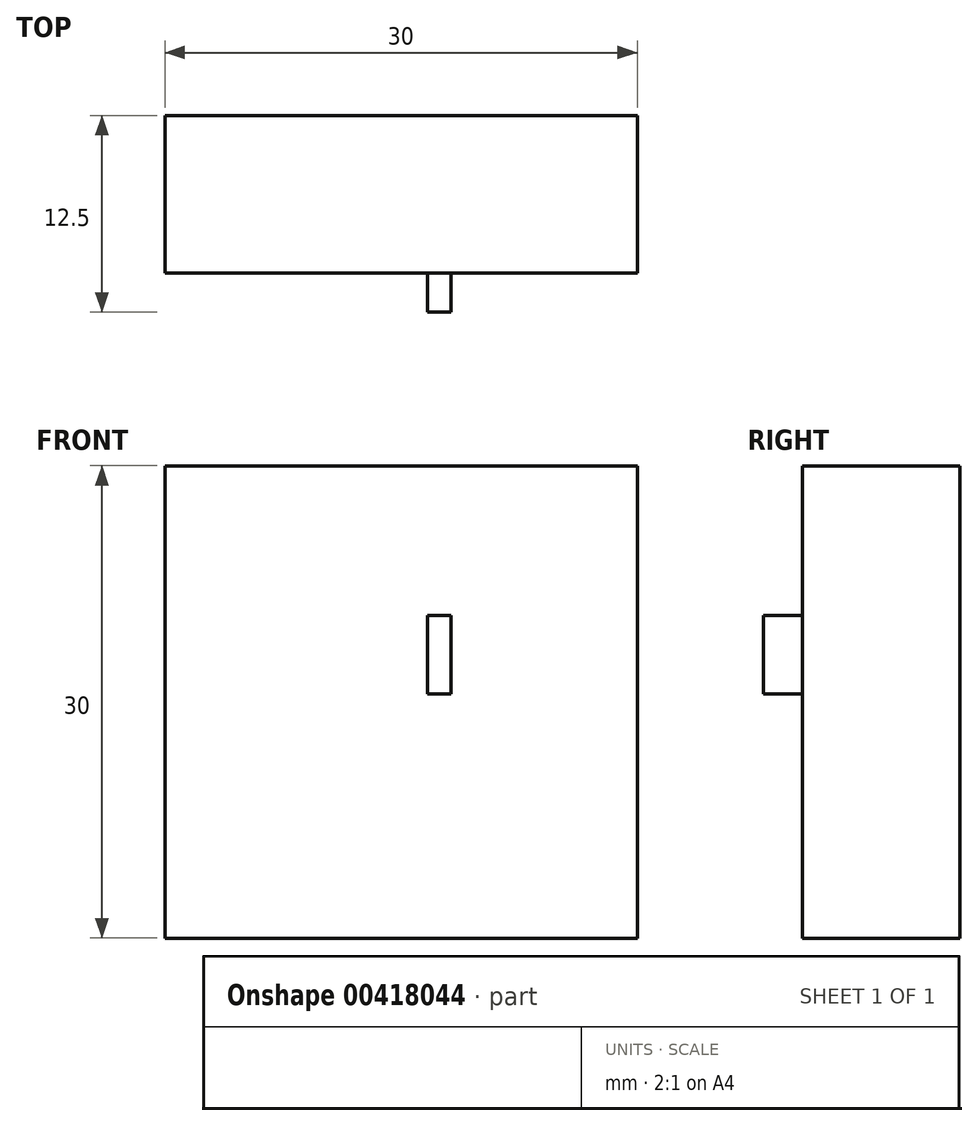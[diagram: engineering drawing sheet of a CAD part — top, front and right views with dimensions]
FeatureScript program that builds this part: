
annotation { "Feature Type Name" : "Feature", "Feature Type Description" : "" }
export const myFeature = defineFeature(function(context is Context, id is Id, definition is map)
    precondition{}
    {
        {
            var Q0;
            Q0=qCreatedBy(makeId("Front.planeOp"),FACE);
            var sketch = newSketch(context, id + "F0", { "sketchPlane" : qUnion([Q0])});
            skLineSegment(sketch, "E0.bottom", {"start": v(-22.95, 34.83) * mm, "end": v(-21.45, 34.83) * mm});
            skLineSegment(sketch, "E0.top", {"start": v(-22.95, 29.83) * mm, "end": v(-21.45, 29.83) * mm});
            skLineSegment(sketch, "E0.left", {"start": v(-22.95, 34.83) * mm, "end": v(-22.95, 29.83) * mm});
            skLineSegment(sketch, "E0.right", {"start": v(-21.45, 34.83) * mm, "end": v(-21.45, 29.83) * mm});
            skSolve(sketch);
        }
        {
            var Q0;
            Q0=makeQuery(id+"F0.imprint","IMPRINT",FACE,{"disambiguationData":[TD([[makeQuery(id+"F0.imprint","IMPRINT",EDGE,{"derivedFrom":sQuery(id+"F0.wireOp",EDGE,"E0.bottom")}),-1.0]])]});
            extrude(context, id + "F1", {"entities" : qUnion([Q0]), "depth" : 2.5 * mm});
        }
        {
            var Q0;
            Q0=qCreatedBy(makeId("Front.planeOp"),FACE);
            var sketch = newSketch(context, id + "F2", { "sketchPlane" : qUnion([Q0])});
            skLineSegment(sketch, "E1.bottom", {"start": v(-39.63, 44.34) * mm, "end": v(-9.63, 44.34) * mm});
            skLineSegment(sketch, "E1.top", {"start": v(-39.63, 14.34) * mm, "end": v(-9.63, 14.34) * mm});
            skLineSegment(sketch, "E1.left", {"start": v(-39.63, 44.34) * mm, "end": v(-39.63, 14.34) * mm});
            skLineSegment(sketch, "E1.right", {"start": v(-9.63, 44.34) * mm, "end": v(-9.63, 14.34) * mm});
            skSolve(sketch);
        }
        {
            var Q0;
            Q0=makeQuery(id+"F2.imprint","IMPRINT",FACE,{"disambiguationData":[TD([[makeQuery(id+"F2.imprint","IMPRINT",EDGE,{"derivedFrom":sQuery(id+"F2.wireOp",EDGE,"E1.bottom")}),-1.0]])]});
            extrude(context, id + "F3", {"entities" : qUnion([Q0]), "operationType" : NewBodyOperationType.ADD, "oppositeDirection" : true, "depth" : 10 * mm});
        }
    });
